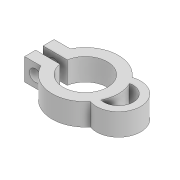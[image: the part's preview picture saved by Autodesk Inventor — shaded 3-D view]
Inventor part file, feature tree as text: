
AUTODESK INVENTOR PART (.ipt)
format: ipt  version: 2022 (Build 260153000, 153)  size: 129,024 bytes
history: native  units: mm
features: extrude x2, sketch x2, projected_geometry x1
ambient origin geometry x8: Origin, YZ Plane, XZ Plane, XY Plane, X Axis, Y Axis, Z Axis, Center Point
bodies: Solid1 (feature_tree)
feature tree (5):
  extrude  "Extrusion1"  Depth=3.0mm
  extrude  "Extrusion2"  Depth=10.0mm
  sketch  "Sketch1"  dims[d0=12.0mm d1=3.0mm]
  sketch  "Sketch2"  dims[d2=3.0mm d3=3.0mm d4=1.0mm d5=1.0mm d6=8.0mm d7=8.0mm d8=8.0mm d9=2.0mm d10=6.0mm d11=0.0mm d12=3.2mm d13=10.0mm d14=0.0mm]
  projected_geometry  "Projected Loop1"
